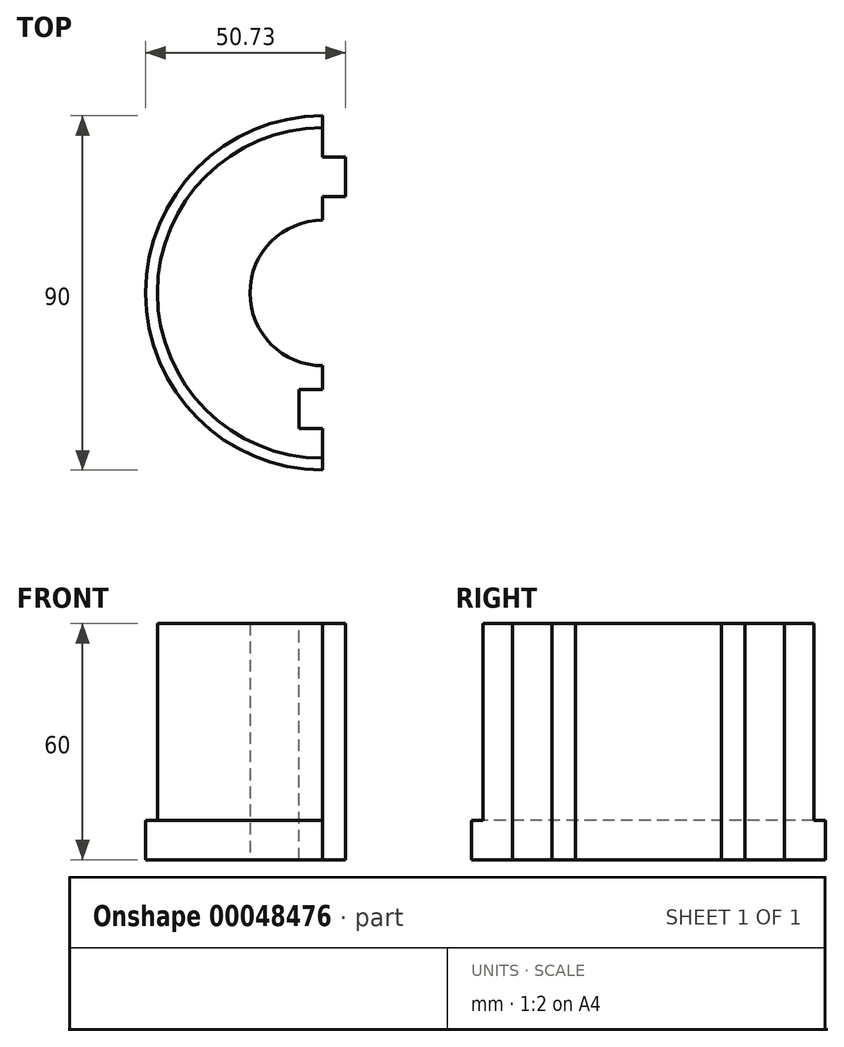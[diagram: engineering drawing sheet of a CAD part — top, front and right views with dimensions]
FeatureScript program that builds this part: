
annotation { "Feature Type Name" : "Feature", "Feature Type Description" : "" }
export const myFeature = defineFeature(function(context is Context, id is Id, definition is map)
    precondition{}
    {
        {
            var Q0;
            Q0=qCreatedBy(makeId("Top.planeOp"),FACE);
            var sketch = newSketch(context, id + "F0", { "sketchPlane" : qUnion([Q0])});
            skCircle(sketch, "E0", {"center": v(0, 0) * mm, "radius": 45 * mm});
            skCircle(sketch, "E1", {"center": v(0, 0) * mm, "radius": 18.5 * mm});
            skSolve(sketch);
        }
        {
            var Q0;
            Q0=makeQuery(id+"F0.imprint","IMPRINT",FACE,{"disambiguationData":[TD([[makeQuery(id+"F0.imprint","IMPRINT",EDGE,{"derivedFrom":sQuery(id+"F0.wireOp",EDGE,"E0")}),1.0]])]});
            extrude(context, id + "F1", {"entities" : qUnion([Q0]), "depth" : 10 * mm});
        }
        {
            var Q0;
            Q0=makeQuery(id+"F1.opExtrude","CAP_FACE",FACE,{"disambiguationData":[OSD([sQuery(id+"F0.wireOp",EDGE,"E0"),sQuery(id+"F0.wireOp",EDGE,"E1")])],"isStart":false});
            var sketch = newSketch(context, id + "F2", { "sketchPlane" : qUnion([Q0])});
            skCircle(sketch, "E2", {"center": v(0, 0) * mm, "radius": 42 * mm});
            skSolve(sketch);
        }
        {
            var Q0;
            Q0=makeQuery(id+"F2.imprint","IMPRINT",FACE,{"disambiguationData":[TD([[makeQuery(id+"F2.imprint","IMPRINT",EDGE,{"derivedFrom":sQuery(id+"F2.wireOp",EDGE,"E2")}),1.0]])]});
            extrude(context, id + "F3", {"entities" : qUnion([Q0]), "operationType" : NewBodyOperationType.ADD, "depth" : 50 * mm});
        }
        {
            var Q0;
            Q0=makeQuery(id+"F3.opExtrude","CAP_FACE",FACE,{"disambiguationData":[OSD([sQuery(id+"F0.wireOp",EDGE,"E1"),sQuery(id+"F2.wireOp",EDGE,"E2")])],"isStart":false});
            var sketch = newSketch(context, id + "F4", { "sketchPlane" : qUnion([Q0])});
            skLineSegment(sketch, "E3", {"start": v(0, 63.32) * mm, "end": v(0, 34.5) * mm});
            skLineSegment(sketch, "E4", {"start": v(0, 34.5) * mm, "end": v(5.73, 34.5) * mm});
            skLineSegment(sketch, "E5", {"start": v(5.73, 34.5) * mm, "end": v(5.73, 24.5) * mm});
            skLineSegment(sketch, "E6", {"start": v(5.73, 24.5) * mm, "end": v(0, 24.5) * mm});
            skLineSegment(sketch, "E7", {"start": v(0, 24.5) * mm, "end": v(0, -24.5) * mm});
            skLineSegment(sketch, "E8", {"start": v(0, -24.5) * mm, "end": v(-6, -24.5) * mm});
            skLineSegment(sketch, "E9", {"start": v(-6, -24.5) * mm, "end": v(-6, -34.5) * mm});
            skLineSegment(sketch, "E10", {"start": v(-6, -34.5) * mm, "end": v(0, -34.5) * mm});
            skLineSegment(sketch, "E11", {"start": v(0, -34.5) * mm, "end": v(0, -52.82) * mm});
            skLineSegment(sketch, "E12", {"start": v(0, -52.82) * mm, "end": v(64.07, -52.82) * mm});
            skLineSegment(sketch, "E13", {"start": v(64.07, -52.82) * mm, "end": v(64.07, 63.32) * mm});
            skLineSegment(sketch, "E14", {"start": v(64.07, 63.32) * mm, "end": v(0, 63.32) * mm});
            skSolve(sketch);
        }
        {
            var Q0;
            {var subQ6=sQuery(id+"F4.wireOp",EDGE,"E12");Q0=makeQuery(id+"F4.imprint","IMPRINT",FACE,{"disambiguationData":[TD([[makeQuery(id+"F4.imprint","IMPRINT",EDGE,{"derivedFrom":subQ6}),1.0]])]});}
            var Q1;
            {var subQ6=sQuery(id+"F4.wireOp",EDGE,"E4");Q1=makeQuery(id+"F4.imprint","IMPRINT",FACE,{"disambiguationData":[TD([[makeQuery(id+"F4.imprint","IMPRINT",EDGE,{"derivedFrom":subQ6}),1.0]])]});}
            extrude(context, id + "F5", {"entities" : qUnion([Q0, Q1]), "operationType" : NewBodyOperationType.REMOVE, "oppositeDirection" : true, "depth" : 79.8 * mm});
        }
    });
